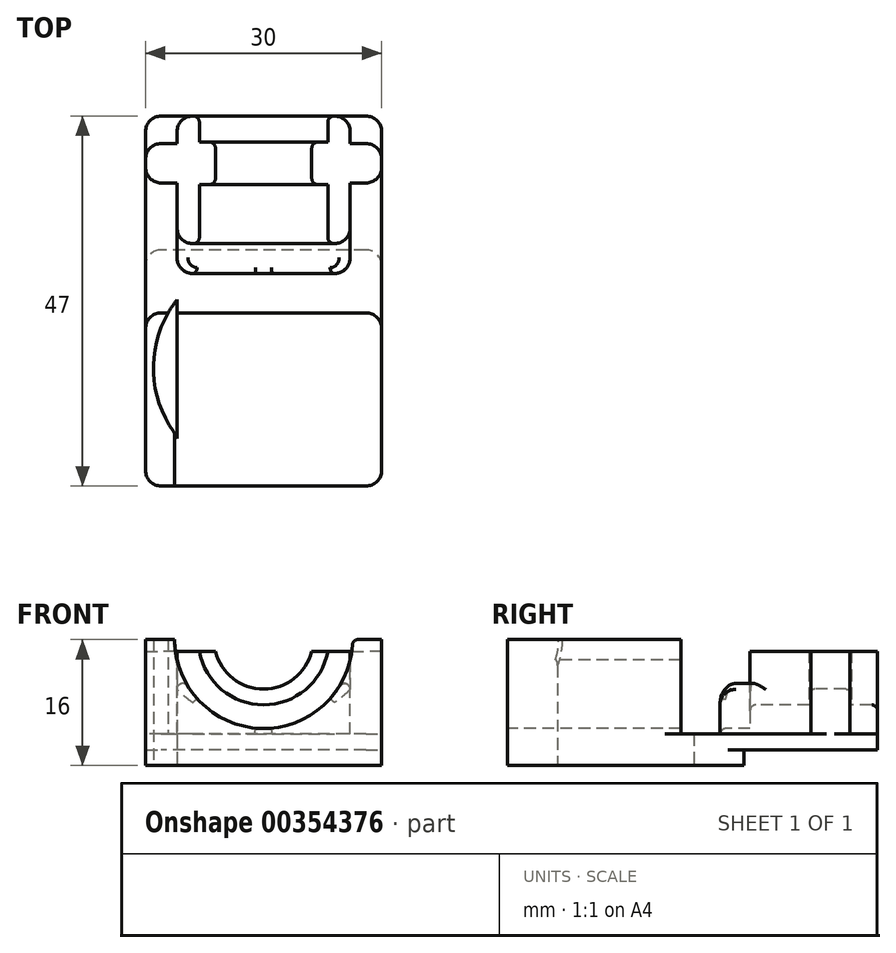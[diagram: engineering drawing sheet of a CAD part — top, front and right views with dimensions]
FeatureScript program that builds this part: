
annotation { "Feature Type Name" : "Feature", "Feature Type Description" : "" }
export const myFeature = defineFeature(function(context is Context, id is Id, definition is map)
    precondition{}
    {
        {
            var Q0;
            Q0=qCreatedBy(makeId("Top.planeOp"),FACE);
            var sketch = newSketch(context, id + "F0", { "sketchPlane" : qUnion([Q0])});
            skLineSegment(sketch, "E0", {"start": v(11, -42.5) * mm, "end": v(11, -16.5) * mm});
            skLineSegment(sketch, "E1", {"start": v(11, -16.5) * mm, "end": v(8, -16.5) * mm});
            skLineSegment(sketch, "E2", {"start": v(8, -16.5) * mm, "end": v(8, -9) * mm});
            skLineSegment(sketch, "E3", {"start": v(8, -9) * mm, "end": v(6, -9) * mm});
            skLineSegment(sketch, "E4", {"start": v(6, -9) * mm, "end": v(6, -3) * mm});
            skLineSegment(sketch, "E5", {"start": v(6, -3) * mm, "end": v(8, -3) * mm});
            skLineSegment(sketch, "E6", {"start": v(8, -3) * mm, "end": v(8, 0) * mm});
            skLineSegment(sketch, "E7", {"start": v(8, 0) * mm, "end": v(0, 0) * mm});
            skLineSegment(sketch, "E8", {"start": v(0, -42.5) * mm, "end": v(0, 0) * mm});
            skLineSegment(sketch, "E9", {"start": v(11, -42.5) * mm, "end": v(0, -42.5) * mm});
            skSolve(sketch);
        }
        {
            var Q0;
            Q0=makeQuery(id+"F0.imprint","IMPRINT",FACE,{"disambiguationData":[TD([[makeQuery(id+"F0.imprint","IMPRINT",EDGE,{"derivedFrom":sQuery(id+"F0.wireOp",EDGE,"E0")}),1.0]])]});
            var Q1;
            Q1=sQuery(id+"F0.wireOp",EDGE,"E8");
            revolve(context, id + "F1", {"entities" : qUnion([Q0]), "axis" : qUnion([Q1]), "revolveType" : RevolveType.FULL});
        }
        {
            var Q0;
            Q0=qCreatedBy(makeId("Front.planeOp"),FACE);
            var sketch = newSketch(context, id + "F2", { "sketchPlane" : qUnion([Q0])});
            skLineSegment(sketch, "E10.bottom", {"start": v(-11, 0) * mm, "end": v(11, 0) * mm});
            skLineSegment(sketch, "E10.top", {"start": v(-11, -12) * mm, "end": v(11, -12) * mm});
            skLineSegment(sketch, "E10.left", {"start": v(-11, -12) * mm, "end": v(-11, 0) * mm});
            skLineSegment(sketch, "E10.right", {"start": v(11, -12) * mm, "end": v(11, 0) * mm});
            skPoint(sketch, "E11", {"position": v(0, 0) * mm});
            skCircle(sketch, "E12.0", {"center": v(0, 0) * mm, "radius": 11 * mm, "construction": true});
            skSolve(sketch);
        }
        {
            var Q0;
            Q0=makeQuery(id+"F2.imprint","IMPRINT",FACE,{"disambiguationData":[TD([[makeQuery(id+"F2.imprint","IMPRINT",EDGE,{"derivedFrom":sQuery(id+"F2.wireOp",EDGE,"E10.bottom")}),-1.0]])]});
            var Q1;
            Q1=makeQuery(id+"F1.opRevolve","SWEPT_FACE",FACE,{"disambiguationData":[OSD([sQuery(id+"F0.wireOp",EDGE,"E1")])]});
            extrude(context, id + "F3", {"entities" : qUnion([Q0]), "endBoundEntityFace" : qUnion([Q1]), "depth" : 20 * mm});
        }
        {
            var Q0;
            Q0=makeQuery(id+"F0.imprint","IMPRINT",FACE,{"disambiguationData":[TD([[makeQuery(id+"F0.imprint","IMPRINT",EDGE,{"derivedFrom":sQuery(id+"F0.wireOp",EDGE,"E0")}),1.0]])]});
            var sketch = newSketch(context, id + "F4", { "sketchPlane" : qUnion([Q0])});
            skLineSegment(sketch, "E13.0.1", {"start": v(11, -42.5) * mm, "end": v(11, -16.5) * mm, "construction": true});
            skLineSegment(sketch, "E13.0.2", {"start": v(11, -16.5) * mm, "end": v(8, -16.5) * mm, "construction": true});
            skLineSegment(sketch, "E13.0.3", {"start": v(8, -16.5) * mm, "end": v(8, -9) * mm, "construction": true});
            skLineSegment(sketch, "E13.0.4", {"start": v(8, -9) * mm, "end": v(6, -9) * mm, "construction": true});
            skLineSegment(sketch, "E13.0.5", {"start": v(6, -9) * mm, "end": v(6, -3) * mm, "construction": true});
            skLineSegment(sketch, "E13.0.6", {"start": v(6, -3) * mm, "end": v(8, -3) * mm, "construction": true});
            skLineSegment(sketch, "E13.0.7", {"start": v(8, -3) * mm, "end": v(8, 0) * mm, "construction": true});
            skLineSegment(sketch, "E14.0", {"start": v(8.3, -3.3) * mm, "end": v(8.3, 0) * mm});
            skLineSegment(sketch, "E14.1", {"start": v(6.3, -3.3) * mm, "end": v(8.3, -3.3) * mm});
            skLineSegment(sketch, "E14.2", {"start": v(6.3, -8.7) * mm, "end": v(6.3, -3.3) * mm});
            skLineSegment(sketch, "E14.3", {"start": v(11.3, -42.5) * mm, "end": v(11.3, -16.2) * mm});
            skLineSegment(sketch, "E14.4", {"start": v(11.3, -16.2) * mm, "end": v(8.3, -16.2) * mm});
            skLineSegment(sketch, "E14.5", {"start": v(8.3, -16.2) * mm, "end": v(8.3, -8.7) * mm});
            skLineSegment(sketch, "E14.6", {"start": v(8.3, -8.7) * mm, "end": v(6.3, -8.7) * mm});
            skLineSegment(sketch, "E15", {"start": v(11.3, -42.5) * mm, "end": v(0, -42.5) * mm});
            skLineSegment(sketch, "E16", {"start": v(8.3, 0) * mm, "end": v(0, 0) * mm, "construction": true});
            skLineSegment(sketch, "E17.1", {"start": v(11, 0) * mm, "end": v(-11, 0) * mm, "construction": true});
            skLineSegment(sketch, "E18", {"start": v(8.3, 0) * mm, "end": v(8.3, 1) * mm});
            skLineSegment(sketch, "E19", {"start": v(0, 1) * mm, "end": v(8.3, 1) * mm});
            skLineSegment(sketch, "E20", {"start": v(0, 1) * mm, "end": v(0, -42.5) * mm});
            skSolve(sketch);
        }
        {
            var Q0;
            Q0 = qSketchRegion(id + "F4", true);
            var Q1;
            Q1=sQuery(id+"F4.wireOp",EDGE,"E20");
            revolve(context, id + "F5", {"operationType" : NewBodyOperationType.REMOVE, "entities" : qUnion([Q0]), "axis" : qUnion([Q1]), "revolveType" : RevolveType.FULL, "oppositeDirection" : true});
        }
        {
            var Q0;
            {var subQ0=sQuery(id+"F2.wireOp",EDGE,"E10.left");var subQ1=sQuery(id+"F2.wireOp",EDGE,"E10.bottom");Q0=makeQuery(id+"F5.boolean.opBoolean","SPLIT",FACE,{"disambiguationData":[TD([makeQuery(id+"F3.opExtrude","SWEPT_FACE",FACE,{"disambiguationData":[OSD([subQ0])]})])],"derivedFrom":makeQuery(id+"F3.opExtrude","SWEPT_FACE",FACE,{"disambiguationData":[OSD([subQ1])]})});}
            var sketch = newSketch(context, id + "F6", { "sketchPlane" : qUnion([Q0])});
            skLineSegment(sketch, "E21.bottom", {"start": v(-11, -8.5) * mm, "end": v(-15, -8.5) * mm});
            skLineSegment(sketch, "E21.top", {"start": v(-11, -3.5) * mm, "end": v(-15, -3.5) * mm});
            skLineSegment(sketch, "E21.left", {"start": v(-11, -8.5) * mm, "end": v(-11, -3.5) * mm});
            skLineSegment(sketch, "E21.right", {"start": v(-15, -8.5) * mm, "end": v(-15, -3.5) * mm});
            skLineSegment(sketch, "E22.MirrorCS", {"start": v(11, -8.5) * mm, "end": v(11, -3.5) * mm});
            skLineSegment(sketch, "E23.MirrorCS", {"start": v(11, -8.5) * mm, "end": v(15, -8.5) * mm});
            skLineSegment(sketch, "E24.MirrorCS", {"start": v(15, -8.5) * mm, "end": v(15, -3.5) * mm});
            skLineSegment(sketch, "E25.MirrorCS", {"start": v(11, -3.5) * mm, "end": v(15, -3.5) * mm});
            skSolve(sketch);
        }
        {
            var Q0;
            Q0 = qSketchRegion(id + "F6", true);
            var Q1;
            Q1=makeQuery(id+"F3.opExtrude","SWEPT_FACE",FACE,{"disambiguationData":[OSD([sQuery(id+"F2.wireOp",EDGE,"E10.top")])]});
            extrude(context, id + "F7", {"entities" : qUnion([Q0]), "operationType" : NewBodyOperationType.ADD, "endBound" : BoundingType.UP_TO_SURFACE, "oppositeDirection" : true, "endBoundEntityFace" : qUnion([Q1]), "depth" : 12 * mm});
        }
        {
            var Q0;
            Q0=makeQuery(id+"F3.opExtrude","SWEPT_FACE",FACE,{"disambiguationData":[OSD([sQuery(id+"F2.wireOp",EDGE,"E10.top")])]});
            var sketch = newSketch(context, id + "F8", { "sketchPlane" : qUnion([Q0])});
            skLineSegment(sketch, "E26.bottom", {"start": v(15, -10) * mm, "end": v(-15, -10) * mm});
            skLineSegment(sketch, "E26.top", {"start": v(15, 5) * mm, "end": v(-15, 5) * mm});
            skLineSegment(sketch, "E26.left", {"start": v(15, -10) * mm, "end": v(15, 5) * mm});
            skLineSegment(sketch, "E26.right", {"start": v(-15, -10) * mm, "end": v(-15, 5) * mm});
            skPoint(sketch, "E27", {"position": v(0, 5) * mm});
            skSolve(sketch);
        }
        {
            var Q0;
            {var subQ5=sQuery(id+"F8.wireOp",EDGE,"E26.top");Q0=makeQuery(id+"F8.imprint","IMPRINT",FACE,{"disambiguationData":[TD([[makeQuery(id+"F8.imprint","IMPRINT",EDGE,{"derivedFrom":subQ5}),-1.0]])]});}
            var sketch = newSketch(context, id + "F9", { "sketchPlane" : qUnion([Q0])});
            skLineSegment(sketch, "E28.bottom", {"start": v(15, 25) * mm, "end": v(-15, 25) * mm});
            skLineSegment(sketch, "E28.top", {"start": v(15, 0) * mm, "end": v(-15, 0) * mm});
            skLineSegment(sketch, "E28.left", {"start": v(15, 25) * mm, "end": v(15, 0) * mm});
            skLineSegment(sketch, "E28.right", {"start": v(-15, 25) * mm, "end": v(-15, 0) * mm});
            skPoint(sketch, "E29", {"position": v(0, 0) * mm});
            skSolve(sketch);
        }
        {
            var Q0;
            Q0 = qSketchRegion(id + "F9", true);
            extrude(context, id + "F10", {"entities" : qUnion([Q0]), "operationType" : NewBodyOperationType.ADD, "depth" : 2 * mm, "offsetDistance" : 25 * mm});
        }
        {
            var Q0;
            Q0=makeQuery(id+"F3.opExtrude","CAP_FACE",FACE,{"disambiguationData":[OSD([sQuery(id+"F2.wireOp",EDGE,"E10.bottom"),sQuery(id+"F2.wireOp",EDGE,"E10.top"),sQuery(id+"F2.wireOp",EDGE,"E10.left"),sQuery(id+"F2.wireOp",EDGE,"E10.right")])],"isStart":true});
            var sketch = newSketch(context, id + "F11", { "sketchPlane" : qUnion([Q0])});
            skLineSegment(sketch, "E30.bottom", {"start": v(-15, 0) * mm, "end": v(15, 0) * mm});
            skLineSegment(sketch, "E30.top", {"start": v(-15, -1.5) * mm, "end": v(15, -1.5) * mm});
            skLineSegment(sketch, "E30.left", {"start": v(-15, 0) * mm, "end": v(-15, -1.5) * mm});
            skLineSegment(sketch, "E30.right", {"start": v(15, 0) * mm, "end": v(15, -1.5) * mm});
            skSolve(sketch);
        }
        {
            var Q0;
            Q0 = qSketchRegion(id + "F11", true);
            extrude(context, id + "F12", {"entities" : qUnion([Q0]), "operationType" : NewBodyOperationType.REMOVE, "endBound" : BoundingType.THROUGH_ALL, "oppositeDirection" : true, "depth" : 25 * mm, "offsetDistance" : 25 * mm});
        }
        {
            var Q0;
            Q0=makeQuery(id+"F10.opExtrude","CAP_FACE",FACE,{"disambiguationData":[OSD([sQuery(id+"F9.wireOp",EDGE,"E28.bottom"),sQuery(id+"F9.wireOp",EDGE,"E28.top"),sQuery(id+"F9.wireOp",EDGE,"E28.left"),sQuery(id+"F9.wireOp",EDGE,"E28.right")])],"isStart":false});
            var sketch = newSketch(context, id + "F13", { "sketchPlane" : qUnion([Q0])});
            skLineSegment(sketch, "E31.bottom", {"start": v(15, 17) * mm, "end": v(-15, 17) * mm});
            skLineSegment(sketch, "E31.top", {"start": v(15, 47) * mm, "end": v(-15, 47) * mm});
            skLineSegment(sketch, "E31.left", {"start": v(15, 17) * mm, "end": v(15, 47) * mm});
            skLineSegment(sketch, "E31.right", {"start": v(-15, 17) * mm, "end": v(-15, 47) * mm});
            skLineSegment(sketch, "E32.0", {"start": v(15, 25) * mm, "end": v(-15, 25) * mm});
            skSolve(sketch);
        }
        {
            var Q0;
            Q0 = qSketchRegion(id + "F13", true);
            extrude(context, id + "F14", {"entities" : qUnion([Q0]), "depth" : 2 * mm, "offsetDistance" : 25 * mm});
        }
        {
            var Q0;
            {var subQ0=sQuery(id+"F13.wireOp",EDGE,"E31.top");Q0=makeQuery(id+"F13.imprint","IMPRINT",FACE,{"disambiguationData":[TD([[makeQuery(id+"F13.imprint","IMPRINT",EDGE,{"derivedFrom":subQ0}),1.0]])]});}
            var Q1;
            Q1=qCreatedBy(makeId("Top.planeOp"),FACE);
            extrude(context, id + "F15", {"entities" : qUnion([Q0]), "operationType" : NewBodyOperationType.ADD, "endBound" : BoundingType.UP_TO_SURFACE, "oppositeDirection" : true, "depth" : 25 * mm, "endBoundEntityFace" : qUnion([Q1]), "offsetDistance" : 25 * mm});
        }
        {
            var Q0;
            {var subQ0=sQuery(id+"F13.wireOp",EDGE,"E31.top");Q0=makeQuery(id+"F15.boolean.opBoolean","MERGE",FACE,{"derivedFrom":[makeQuery(id+"F14.opExtrude","SWEPT_FACE",FACE,{"disambiguationData":[OSD([subQ0])]}),makeQuery(id+"F15.opExtrude","SWEPT_FACE",FACE,{"disambiguationData":[OSD([subQ0])]})]});}
            var sketch = newSketch(context, id + "F16", { "sketchPlane" : qUnion([Q0])});
            skCircle(sketch, "E33.0", {"center": v(0, 0) * mm, "radius": 11 * mm, "construction": true});
            skCircle(sketch, "E34.0", {"center": v(0, 0) * mm, "radius": 11.3 * mm});
            skSolve(sketch);
        }
        {
            var Q0;
            {var subQ0=sQuery(id+"F16.wireOp",EDGE,"E34.0");var subQ1=makeQuery(id+"F15.opExtrude","TWEAK_EDGE",EDGE,{"derivedFrom":[dummyQuery(id+"Top.planeOp",FACE),makeQuery(id+"F13.imprint","IMPRINT",EDGE,{"derivedFrom":sQuery(id+"F13.wireOp",EDGE,"E31.top")})]});var subQ2=makeQuery(id+"F16.imprint","INTERSECT",VERTEX,{"disambiguationData":[OD(0.0)],"derivedFrom":[subQ1,subQ0]});Q0=makeQuery(id+"F16.imprint","IMPRINT",FACE,{"disambiguationData":[TD([[makeQuery(id+"F16.imprint","IMPRINT",EDGE,{"disambiguationData":[TD([[subQ2,1.0]])],"derivedFrom":subQ0}),1.0]])]});}
            var Q1;
            Q1=sQuery(id+"F16.wireOp",EDGE,"E34.0");
            var Q2;
            Q2=makeQuery(id+"F15.opExtrude","SWEPT_FACE",FACE,{"disambiguationData":[OSD([sQuery(id+"F13.wireOp",EDGE,"E32.0")])]});
            extrude(context, id + "F17", {"entities" : qUnion([Q0]), "operationType" : NewBodyOperationType.REMOVE, "surfaceEntities" : qUnion([Q1]), "endBound" : BoundingType.UP_TO_SURFACE, "oppositeDirection" : true, "depth" : 25 * mm, "endBoundEntityFace" : qUnion([Q2]), "offsetDistance" : 25 * mm});
        }
        {
            var Q0;
            Q0=makeQuery(id+"F14.opExtrude","CAP_FACE",FACE,{"disambiguationData":[OSD([sQuery(id+"F13.wireOp",EDGE,"E31.bottom"),sQuery(id+"F13.wireOp",EDGE,"E31.top"),sQuery(id+"F13.wireOp",EDGE,"E31.left"),sQuery(id+"F13.wireOp",EDGE,"E31.right")])],"isStart":false});
            var sketch = newSketch(context, id + "F18", { "sketchPlane" : qUnion([Q0])});
            skLineSegment(sketch, "E35", {"start": v(15, 17) * mm, "end": v(-15, 47) * mm, "construction": true});
            skPoint(sketch, "E36", {"position": v(0, 32) * mm});
            skCircle(sketch, "E37", {"center": v(0, 32) * mm, "radius": 14 * mm});
            skLineSegment(sketch, "E38.bottom", {"start": v(11, 17) * mm, "end": v(-11, 17) * mm});
            skLineSegment(sketch, "E38.top", {"start": v(11, 47) * mm, "end": v(-11, 47) * mm});
            skLineSegment(sketch, "E38.left", {"start": v(-11, 17) * mm, "end": v(-11, 47) * mm});
            skLineSegment(sketch, "E38.right", {"start": v(11, 17) * mm, "end": v(11, 47) * mm});
            skPoint(sketch, "E39", {"position": v(0, 17) * mm});
            skLineSegment(sketch, "E40", {"start": v(15, 23) * mm, "end": v(-15, 23) * mm});
            skSolve(sketch);
        }
        {
            var Q0;
            {var subQ0=sQuery(id+"F18.wireOp",EDGE,"E38.left");var subQ1=sQuery(id+"F18.wireOp",EDGE,"E37");var subQ2=makeQuery(id+"F18.imprint","INTERSECT",VERTEX,{"disambiguationData":[OD(0.0)],"derivedFrom":[subQ1,subQ0]});Q0=makeQuery(id+"F18.imprint","IMPRINT",FACE,{"disambiguationData":[TD([[makeQuery(id+"F18.imprint","IMPRINT",EDGE,{"disambiguationData":[TD([[subQ2,1.0]])],"derivedFrom":subQ1}),1.0]])]});}
            extrude(context, id + "F19", {"entities" : qUnion([Q0]), "operationType" : NewBodyOperationType.REMOVE, "oppositeDirection" : true, "depth" : 25 * mm, "offsetDistance" : 25 * mm});
        }
        {
            var Q0;
            Q0=makeQuery(id+"F3.opExtrude","CAP_EDGE",EDGE,{"disambiguationData":[OSD([sQuery(id+"F2.wireOp",EDGE,"E10.right")])],"isStart":false});
            var Q1;
            Q1=makeQuery(id+"F3.opExtrude","CAP_EDGE",EDGE,{"disambiguationData":[OSD([sQuery(id+"F2.wireOp",EDGE,"E10.right")])],"isStart":true});
            var Q2;
            Q2=makeQuery(id+"F3.opExtrude","CAP_EDGE",EDGE,{"disambiguationData":[OSD([sQuery(id+"F2.wireOp",EDGE,"E10.left")])],"isStart":true});
            var Q3;
            Q3=makeQuery(id+"F3.opExtrude","CAP_EDGE",EDGE,{"disambiguationData":[OSD([sQuery(id+"F2.wireOp",EDGE,"E10.left")])],"isStart":false});
            var Q4;
            Q4=makeQuery(id+"F5.boolean.opBoolean","INTERSECT",EDGE,{"derivedFrom":[makeQuery(id+"F3.opExtrude","SWEPT_FACE",FACE,{"disambiguationData":[OSD([sQuery(id+"F2.wireOp",EDGE,"E10.left")])]}),makeQuery(id+"F5.opRevolve","SWEPT_FACE",FACE,{"disambiguationData":[OSD([sQuery(id+"F4.wireOp",EDGE,"E14.4")])]})]});
            var Q5;
            Q5=makeQuery(id+"F5.boolean.opBoolean","INTERSECT",EDGE,{"derivedFrom":[makeQuery(id+"F3.opExtrude","SWEPT_FACE",FACE,{"disambiguationData":[OSD([sQuery(id+"F2.wireOp",EDGE,"E10.right")])]}),makeQuery(id+"F5.opRevolve","SWEPT_FACE",FACE,{"disambiguationData":[OSD([sQuery(id+"F4.wireOp",EDGE,"E14.4")])]})]});
            var Q6;
            Q6=makeQuery(id+"FC6LZ2jClKCHcoI_2.opExtrude","SWEPT_EDGE",EDGE,{"disambiguationData":[OSD([sQuery(id+"F8.wireOp",EDGE,"E26.bottom"),sQuery(id+"F8.wireOp",EDGE,"E26.left")])]});
            var Q7;
            Q7=makeQuery(id+"FC6LZ2jClKCHcoI_2.opExtrude","SWEPT_EDGE",EDGE,{"disambiguationData":[OSD([sQuery(id+"F8.wireOp",EDGE,"E26.bottom"),sQuery(id+"F8.wireOp",EDGE,"E26.right")])]});
            var Q8;
            Q8=makeQuery(id+"F7.opExtrude","SWEPT_EDGE",EDGE,{"disambiguationData":[OSD([sQuery(id+"F6.wireOp",EDGE,"E21.bottom"),sQuery(id+"F6.wireOp",EDGE,"E21.right")])]});
            var Q9;
            Q9=makeQuery(id+"F7.opExtrude","SWEPT_EDGE",EDGE,{"disambiguationData":[OSD([sQuery(id+"F6.wireOp",EDGE,"E23.MirrorCS"),sQuery(id+"F6.wireOp",EDGE,"E24.MirrorCS")])]});
            var Q10;
            Q10=makeQuery(id+"F7.opExtrude","SWEPT_EDGE",EDGE,{"disambiguationData":[OSD([sQuery(id+"F6.wireOp",EDGE,"E24.MirrorCS"),sQuery(id+"F6.wireOp",EDGE,"E25.MirrorCS")])]});
            var Q11;
            Q11=makeQuery(id+"F7.opExtrude","SWEPT_EDGE",EDGE,{"disambiguationData":[OSD([sQuery(id+"F6.wireOp",EDGE,"E21.top"),sQuery(id+"F6.wireOp",EDGE,"E21.right")])]});
            var Q12;
            Q12=makeQuery(id+"F10.opExtrude","SWEPT_EDGE",EDGE,{"disambiguationData":[OSD([sQuery(id+"F9.wireOp",EDGE,"E28.top"),sQuery(id+"F9.wireOp",EDGE,"E28.left")])]});
            var Q13;
            Q13=makeQuery(id+"F10.opExtrude","SWEPT_EDGE",EDGE,{"disambiguationData":[OSD([sQuery(id+"F9.wireOp",EDGE,"E28.top"),sQuery(id+"F9.wireOp",EDGE,"E28.right")])]});
            var Q14;
            Q14=makeQuery(id+"F14.opExtrude","SWEPT_EDGE",EDGE,{"disambiguationData":[OSD([sQuery(id+"F9.wireOp",EDGE,"E28.right"),sQuery(id+"F13.wireOp",EDGE,"E31.bottom"),sQuery(id+"F13.wireOp",EDGE,"E31.right")])]});
            var Q15;
            Q15=makeQuery(id+"F14.opExtrude","SWEPT_EDGE",EDGE,{"disambiguationData":[OSD([sQuery(id+"F9.wireOp",EDGE,"E28.left"),sQuery(id+"F13.wireOp",EDGE,"E31.bottom"),sQuery(id+"F13.wireOp",EDGE,"E31.left")])]});
            var Q16;
            Q16=makeQuery(id+"F15.opExtrude","SWEPT_EDGE",EDGE,{"disambiguationData":[OSD([sQuery(id+"F13.wireOp",EDGE,"E31.left"),sQuery(id+"F13.wireOp",EDGE,"E32.0")])]});
            var Q17;
            Q17=makeQuery(id+"F15.opExtrude","SWEPT_EDGE",EDGE,{"disambiguationData":[OSD([sQuery(id+"F13.wireOp",EDGE,"E31.right"),sQuery(id+"F13.wireOp",EDGE,"E32.0")])]});
            var Q18;
            {var subQ0=sQuery(id+"F13.wireOp",EDGE,"E31.right");var subQ1=sQuery(id+"F13.wireOp",EDGE,"E31.top");Q18=makeQuery(id+"F15.boolean.opBoolean","MERGE",EDGE,{"derivedFrom":[makeQuery(id+"F14.opExtrude","SWEPT_EDGE",EDGE,{"disambiguationData":[OSD([subQ1,subQ0])]}),makeQuery(id+"F15.opExtrude","SWEPT_EDGE",EDGE,{"disambiguationData":[OSD([subQ1,subQ0])]})]});}
            var Q19;
            {var subQ0=sQuery(id+"F13.wireOp",EDGE,"E31.left");var subQ1=sQuery(id+"F13.wireOp",EDGE,"E31.top");Q19=makeQuery(id+"F15.boolean.opBoolean","MERGE",EDGE,{"derivedFrom":[makeQuery(id+"F14.opExtrude","SWEPT_EDGE",EDGE,{"disambiguationData":[OSD([subQ1,subQ0])]}),makeQuery(id+"F15.opExtrude","SWEPT_EDGE",EDGE,{"disambiguationData":[OSD([subQ1,subQ0])]})]});}
            var Q20;
            Q20=makeQuery(id+"F10.opExtrude","SWEPT_EDGE",EDGE,{"disambiguationData":[OSD([sQuery(id+"F9.wireOp",EDGE,"E28.bottom"),sQuery(id+"F9.wireOp",EDGE,"E28.left")])]});
            var Q21;
            Q21=makeQuery(id+"F10.opExtrude","SWEPT_EDGE",EDGE,{"disambiguationData":[OSD([sQuery(id+"F9.wireOp",EDGE,"E28.bottom"),sQuery(id+"F9.wireOp",EDGE,"E28.right")])]});
            fillet(context, id + "F20", {"entities" : qUnion([Q0, Q1, Q2, Q3, Q4, Q5, Q6, Q7, Q8, Q9, Q10, Q11, Q12, Q13, Q14, Q15, Q16, Q17, Q18, Q19, Q20, Q21]), "radius" : 2 * mm, "tangentPropagation" : true, "allowEdgeOverflow" : false});
        }
        {
            var Q0;
            Q0=makeQuery(id+"F5.boolean.opBoolean","COPY",EDGE,{"derivedFrom":makeQuery(id+"F5.opRevolve","SWEPT_EDGE",EDGE,{"disambiguationData":[OSD([sQuery(id+"F4.wireOp",EDGE,"E14.1"),sQuery(id+"F4.wireOp",EDGE,"E14.2")])]})});
            var Q1;
            Q1=makeQuery(id+"F5.boolean.opBoolean","COPY",EDGE,{"derivedFrom":makeQuery(id+"F5.opRevolve","SWEPT_EDGE",EDGE,{"disambiguationData":[OSD([sQuery(id+"F4.wireOp",EDGE,"E14.2"),sQuery(id+"F4.wireOp",EDGE,"E14.6")])]})});
            var Q2;
            Q2=makeQuery(id+"F5.boolean.opBoolean","COPY",EDGE,{"derivedFrom":makeQuery(id+"F5.opRevolve","SWEPT_EDGE",EDGE,{"disambiguationData":[OSD([sQuery(id+"F4.wireOp",EDGE,"E14.4"),sQuery(id+"F4.wireOp",EDGE,"E14.5")])]})});
            var Q3;
            Q3=makeQuery(id+"F5.boolean.opBoolean","INTERSECT",EDGE,{"derivedFrom":[makeQuery(id+"F3.opExtrude","CAP_FACE",FACE,{"disambiguationData":[OSD([sQuery(id+"F2.wireOp",EDGE,"E10.bottom"),sQuery(id+"F2.wireOp",EDGE,"E10.top"),sQuery(id+"F2.wireOp",EDGE,"E10.left"),sQuery(id+"F2.wireOp",EDGE,"E10.right")])],"isStart":true}),makeQuery(id+"F5.opRevolve","SWEPT_FACE",FACE,{"disambiguationData":[OSD([sQuery(id+"F4.wireOp",EDGE,"E14.0"),sQuery(id+"F4.wireOp",EDGE,"E18")])]})]});
            var Q4;
            Q4=makeQuery(id+"F5.boolean.opBoolean","INTERSECT",EDGE,{"derivedFrom":[makeQuery(id+"F3.opExtrude","CAP_FACE",FACE,{"disambiguationData":[OSD([sQuery(id+"F2.wireOp",EDGE,"E10.bottom"),sQuery(id+"F2.wireOp",EDGE,"E10.top"),sQuery(id+"F2.wireOp",EDGE,"E10.left"),sQuery(id+"F2.wireOp",EDGE,"E10.right")])],"isStart":false}),makeQuery(id+"F5.opRevolve","SWEPT_FACE",FACE,{"disambiguationData":[OSD([sQuery(id+"F4.wireOp",EDGE,"E14.3")])]})]});
            var Q5;
            Q5=makeQuery(id+"F5.boolean.opBoolean","INTERSECT",EDGE,{"disambiguationData":[OD(0.0)],"derivedFrom":[makeQuery(id+"F3.opExtrude","SWEPT_FACE",FACE,{"disambiguationData":[OSD([sQuery(id+"F2.wireOp",EDGE,"E10.bottom")])]}),makeQuery(id+"F5.opRevolve","SWEPT_FACE",FACE,{"disambiguationData":[OSD([sQuery(id+"F4.wireOp",EDGE,"E14.5")])]})]});
            var Q6;
            Q6=makeQuery(id+"F5.boolean.opBoolean","INTERSECT",EDGE,{"disambiguationData":[OD(0.0)],"derivedFrom":[makeQuery(id+"F3.opExtrude","SWEPT_FACE",FACE,{"disambiguationData":[OSD([sQuery(id+"F2.wireOp",EDGE,"E10.bottom")])]}),makeQuery(id+"F5.opRevolve","SWEPT_FACE",FACE,{"disambiguationData":[OSD([sQuery(id+"F4.wireOp",EDGE,"E14.0"),sQuery(id+"F4.wireOp",EDGE,"E18")])]})]});
            var Q7;
            Q7=makeQuery(id+"F5.boolean.opBoolean","INTERSECT",EDGE,{"disambiguationData":[OD(0.0)],"derivedFrom":[makeQuery(id+"F3.opExtrude","SWEPT_FACE",FACE,{"disambiguationData":[OSD([sQuery(id+"F2.wireOp",EDGE,"E10.bottom")])]}),makeQuery(id+"F5.opRevolve","SWEPT_FACE",FACE,{"disambiguationData":[OSD([sQuery(id+"F4.wireOp",EDGE,"E14.2")])]})]});
            var Q8;
            Q8=makeQuery(id+"F5.boolean.opBoolean","INTERSECT",EDGE,{"disambiguationData":[OD(1.0)],"derivedFrom":[makeQuery(id+"F3.opExtrude","SWEPT_FACE",FACE,{"disambiguationData":[OSD([sQuery(id+"F2.wireOp",EDGE,"E10.bottom")])]}),makeQuery(id+"F5.opRevolve","SWEPT_FACE",FACE,{"disambiguationData":[OSD([sQuery(id+"F4.wireOp",EDGE,"E14.5")])]})]});
            var Q9;
            Q9=makeQuery(id+"F5.boolean.opBoolean","INTERSECT",EDGE,{"disambiguationData":[OD(1.0)],"derivedFrom":[makeQuery(id+"F3.opExtrude","SWEPT_FACE",FACE,{"disambiguationData":[OSD([sQuery(id+"F2.wireOp",EDGE,"E10.bottom")])]}),makeQuery(id+"F5.opRevolve","SWEPT_FACE",FACE,{"disambiguationData":[OSD([sQuery(id+"F4.wireOp",EDGE,"E14.2")])]})]});
            var Q10;
            Q10=makeQuery(id+"F5.boolean.opBoolean","INTERSECT",EDGE,{"disambiguationData":[OD(1.0)],"derivedFrom":[makeQuery(id+"F3.opExtrude","SWEPT_FACE",FACE,{"disambiguationData":[OSD([sQuery(id+"F2.wireOp",EDGE,"E10.bottom")])]}),makeQuery(id+"F5.opRevolve","SWEPT_FACE",FACE,{"disambiguationData":[OSD([sQuery(id+"F4.wireOp",EDGE,"E14.0"),sQuery(id+"F4.wireOp",EDGE,"E18")])]})]});
            var Q11;
            Q11=makeQuery(id+"FC6LZ2jClKCHcoI_2.opExtrude","CAP_EDGE",EDGE,{"disambiguationData":[OSD([sQuery(id+"F8.wireOp",EDGE,"E26.bottom")])],"isStart":false});
            var Q12;
            {var subQ0=sQuery(id+"F16.wireOp",EDGE,"E34.0");var subQ1=sQuery(id+"F13.wireOp",EDGE,"E31.top");var subQ2=dummyQuery(id+"Top.planeOp",FACE);Q12=makeQuery(id+"F17.boolean.opBoolean","COPY",EDGE,{"derivedFrom":makeQuery(id+"F17.opExtrude","SWEPT_EDGE",EDGE,{"disambiguationData":[OSD([subQ2,subQ1,subQ0]),TDD([makeQuery(id+"F16.imprint","INTERSECT",VERTEX,{"disambiguationData":[OD(1.0)],"derivedFrom":[makeQuery(id+"F15.opExtrude","TWEAK_EDGE",EDGE,{"derivedFrom":[subQ2,makeQuery(id+"F13.imprint","IMPRINT",EDGE,{"derivedFrom":subQ1})]}),subQ0]})])]})});}
            var Q13;
            {var subQ0=sQuery(id+"F16.wireOp",EDGE,"E34.0");var subQ1=sQuery(id+"F13.wireOp",EDGE,"E31.top");var subQ2=dummyQuery(id+"Top.planeOp",FACE);Q13=makeQuery(id+"F17.boolean.opBoolean","COPY",EDGE,{"derivedFrom":makeQuery(id+"F17.opExtrude","SWEPT_EDGE",EDGE,{"disambiguationData":[OSD([subQ2,subQ1,subQ0]),TDD([makeQuery(id+"F16.imprint","INTERSECT",VERTEX,{"disambiguationData":[OD(0.0)],"derivedFrom":[makeQuery(id+"F15.opExtrude","TWEAK_EDGE",EDGE,{"derivedFrom":[subQ2,makeQuery(id+"F13.imprint","IMPRINT",EDGE,{"derivedFrom":subQ1})]}),subQ0]})])]})});}
            var Q14;
            {var subQ0=sQuery(id+"F18.wireOp",EDGE,"E37");Q14=makeQuery(id+"F19.boolean.opBoolean","INTERSECT",EDGE,{"derivedFrom":[makeQuery(id+"F17.boolean.opBoolean","COPY",FACE,{"derivedFrom":makeQuery(id+"F17.opExtrude","SWEPT_FACE",FACE,{"disambiguationData":[OSD([sQuery(id+"F16.wireOp",EDGE,"E34.0")])]})}),makeQuery(id+"F19.opExtrude","SWEPT_FACE",FACE,{"disambiguationData":[OSD([subQ0]),TDD([makeQuery(id+"F18.imprint","IMPRINT",EDGE,{"disambiguationData":[TD([[makeQuery(id+"F18.imprint","INTERSECT",VERTEX,{"disambiguationData":[OD(0.0)],"derivedFrom":[subQ0,sQuery(id+"F18.wireOp",EDGE,"E38.left")]}),1.0]])],"derivedFrom":subQ0})])]})]});}
            fillet(context, id + "F21", {"entities" : qUnion([Q0, Q1, Q2, Q3, Q4, Q5, Q6, Q7, Q8, Q9, Q10, Q11, Q12, Q13, Q14]), "radius" : 0.75 * mm, "tangentPropagation" : true, "allowEdgeOverflow" : false});
        }
    });
